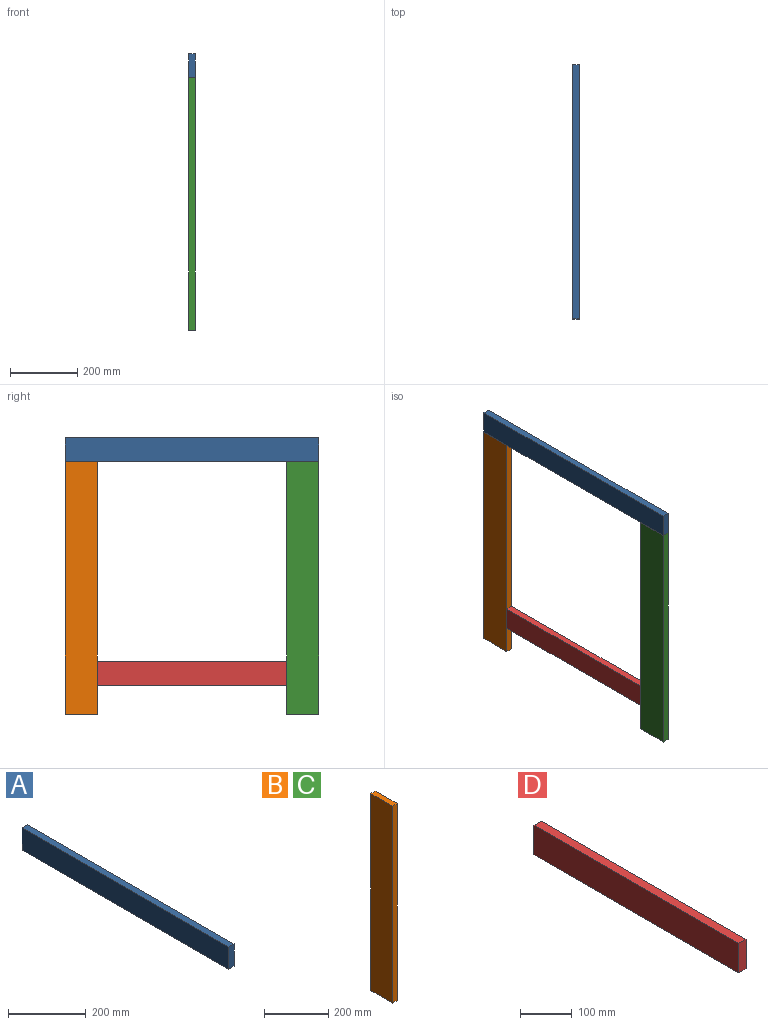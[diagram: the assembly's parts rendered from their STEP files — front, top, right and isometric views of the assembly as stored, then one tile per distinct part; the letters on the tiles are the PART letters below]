
ASSEMBLY  parts=4 mates=3
PART A: 6 faces, bbox 20x753x70 mm
  f0: plane 753x20mm, normal (0,0,1), area 15060mm2, adj f1,f3,f4,f5
  f1: plane 753x70mm, normal (1,0,0), area 52710mm2, adj f0,f2,f4,f5
  f2: plane 753x20mm, normal (0,0,-1), area 15060mm2, adj f1,f3,f4,f5
  f3: plane 753x70mm, normal (-1,0,0), area 52710mm2, adj f0,f2,f4,f5
  f4: plane 70x20mm, normal (0,-1,0), area 1400mm2, adj f0,f1,f2,f3
  f5: plane 70x20mm, normal (0,1,0), area 1400mm2, adj f0,f1,f2,f3
PART B: 6 faces, bbox 20x96x750 mm
  f0: plane 750x96mm, normal (1,0,0), area 72000mm2, adj f1,f3,f4,f5
  f1: plane 750x20mm, normal (0,1,0), area 15000mm2, adj f0,f2,f4,f5
  f2: plane 750x96mm, normal (-1,0,0), area 72000mm2, adj f1,f3,f4,f5
  f3: plane 750x20mm, normal (0,-1,0), area 15000mm2, adj f0,f2,f4,f5
  f4: plane 96x20mm, normal (0,0,1), area 1920mm2, adj f0,f1,f2,f3
  f5: plane 96x20mm, normal (0,0,-1), area 1920mm2, adj f0,f1,f2,f3
PART C: same geometry as B
PART D: 6 faces, bbox 20x561x70 mm
  f0: plane 70x20mm, normal (0,-1,0), area 1400mm2, adj f1,f3,f4,f5
  f1: plane 561x20mm, normal (0,0,-1), area 11220mm2, adj f0,f2,f3,f4
  f2: plane 70x20mm, normal (0,1,0), area 1400mm2, adj f1,f3,f4,f5
  f3: plane 561x70mm, normal (1,0,0), area 39270mm2, adj f0,f1,f2,f5
  f4: plane 561x70mm, normal (-1,0,0), area 39270mm2, adj f0,f1,f2,f5
  f5: plane 561x20mm, normal (0,0,1), area 11220mm2, adj f0,f2,f3,f4
PLACE A t=(0,-33,0)mm
PLACE B t=(0,-33,0)mm
PLACE C t=(0,-690,0)mm
PLACE D t=(0,-33,0)mm
MATE fastened D.f3 <-> C.f0  axis (1,0,0) through (0,-657,85)mm
MATE fastened B.f0 <-> A.f1  axis (1,0,0) through (0,0,750)mm
MATE fastened D.f3 <-> B.f0  axis (1,0,0) through (0,-96,85)mm
